# Revit family: Enveloppe industrielle armoire Marina porte pleine
name_source: partatom
category: Equipement électrique
units: mm (PartAtom-declared; Revit-internal decimal feet)

## family parameters
Basée sur le plan de construction = Non
Configuration du panneau = Deux colonnes, circuits au sein
Cote de connecteur circulaire = Utiliser le diamètre
Couper avec des vides une fois chargée = Non
Numéro OmniClass = 23.80.30.11.17
Partagée = Non
Point de calcul de pièce = Non
Titre OmniClass = Distribution Boards and Control Panels
Toujours verticalement = Oui
Type d'élément = Tableau de raccordement

## types (3) — shared parameters
Commentaires du type = Legrand
Conditions Générale d'Utilisation = https://export.legrand.com
ETIM Class 6.0 = EC000058
IK = 10
IP = 66
Image du type = Armoire_marina_036286_pw_92785_pz_1.jpg
Largeur = 800 mm  [stored 2.62467 ft]
Largeur zone d'installation = 1726 mm
Matière = Polyester
RAL = 7035
URL = www.legrand.fr
distance avant zone d'installation = 800 mm  [stored 2.62467 ft]
distance coté zone d'installation = 463 mm  [stored 1.51903 ft]
profondeur = 463 mm  [stored 1.51903 ft]
profondeur zone d'installation = 1263 mm  [stored 4.1437 ft]
zero-valued in all types: Elévation par défaut

## per-type parameters (varying)
| type | Armoire 036285 | Armoire 036286 | Armoire 036287 | Description | Hauteur | Poids |
| Armoire Marina profondeur 400 hauteur 1400 largeur 800 | Oui | Non | Non | 036285  Armoire Marina profondeur 400 hauteur 1400 largeur 800 | 1460 mm  [stored 4.79003 ft] | 49.00 kg |
| Armoire Marina profondeur 400 hauteur 1600 largeur 800 | Non | Oui | Non | 036286   Armoire Marina profondeur 400 hauteur 1600 largeur 800 | 1660 mm  [stored 5.44619 ft] | 53.00 kg |
| Armoire Marina profondeur 400 hauteur 1800 largeur 800 | Non | Non | Oui | 036287   Armoire Marina profondeur 400 hauteur 1800 largeur 800 | 1860 mm  [stored 6.10236 ft] | 57.00 kg |

note: [stored X ft] marks values corroborated as IEEE doubles in the binary element streams (Revit-internal decimal feet)
